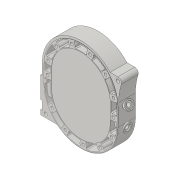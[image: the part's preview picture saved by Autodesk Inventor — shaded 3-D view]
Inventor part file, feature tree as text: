
AUTODESK INVENTOR PART (.ipt)
format: ipt  version: 2016 (Build 200138000, 138)  size: 543,744 bytes
history: native  units: in
note: dims shown in document units (in); Inventor stores cm internally (conversion verified against a paired STEP export)
features: thread x4
ambient origin geometry x8: Origin, YZ Plane, XZ Plane, XY Plane, X Axis, Y Axis, Z Axis, Center Point
bodies: Solid2 (feature_tree), Solid1 (feature_tree)
feature tree (4):
  thread  "Thread1"  [1 undecoded]
  thread  "Thread2"  [1 undecoded]
  thread  "Thread3"  [1 undecoded]
  thread  "Thread4"  [1 undecoded]
note: 4 required parameter values undecoded (feature->parameter linkage not recoverable at this tier; creation-order binding heuristic only, values carry confidence <= 0.55)
